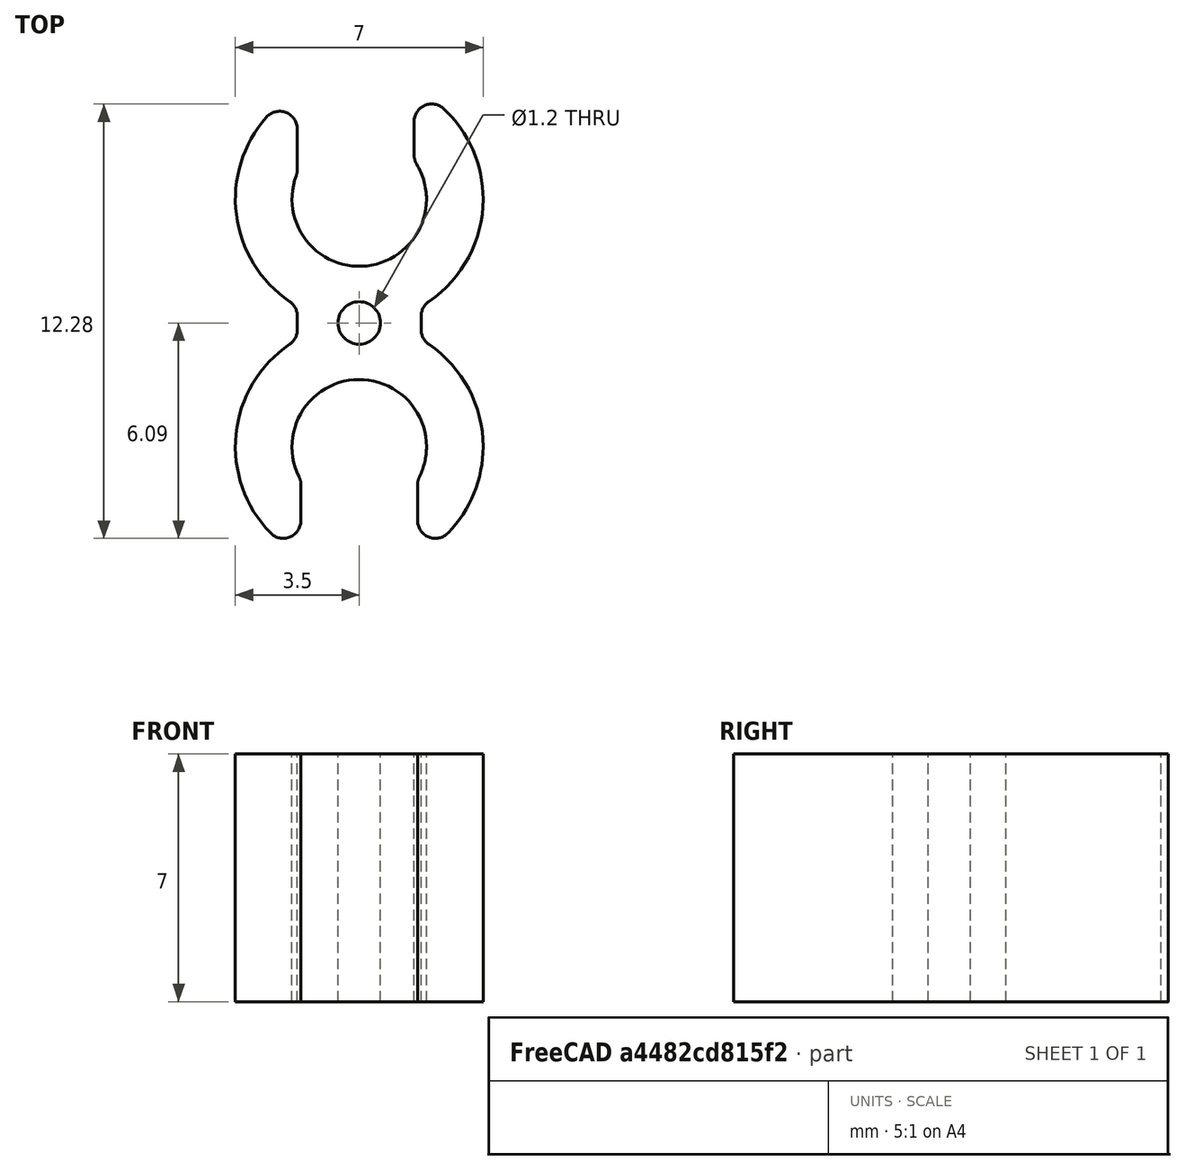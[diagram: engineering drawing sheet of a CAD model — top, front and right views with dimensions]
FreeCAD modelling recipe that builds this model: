
FCSTD DOCUMENT  (FreeCAD 0.15R4671 (Git))
Label: double_link
License: All rights reserved
LicenseURL: http://en.wikipedia.org/wiki/All_rights_reserved
objects: Part::Cut×4, Part::Cylinder×3, Part::Box×3, Part::MultiFuse×2, Part::FeaturePython×1, Part::Fillet×1
note: 14 computed .brp shape members not serialized (recipe doc carries the construction recipe); baked Part::Feature solids carry a one-line shape summary decoded from their .brp

FEATURE [Part::Cylinder] Cylinder  label="base_cylinder"
  Angle = 360
  Height = 7
  Radius = 3.5
FEATURE [Part::Cylinder] Cylinder001  label="base_cylinder_hole"
  Angle = 360
  Height = 10
  Placement = pos=(0,0,-1) rot=(0,0,1;0rad)
  Radius = 1.9
FEATURE [Part::Cut] Cut  label="cylinder_with_hole"
  Base = -> Cylinder
  Tool = -> Cylinder001
FEATURE [Part::FeaturePython] Clone  label="cylinder_with_hole2"  # Draft clone (typed FeaturePython)
  Objects = -> [Cut]
  Placement = pos=(0,7,0) rot=(0,0,1;0rad)
  Scale = (1,1,1)
FEATURE [Part::Box] Box  label="cylinder_open_section"
  Height = 10
  Length = 3.3
  Placement = pos=(-1.65,-10,-2) rot=(0,0,1;0rad)
  Width = 10
FEATURE [Part::Box] Box001  label="cylinder_open_section2"
  Height = 10
  Length = 3.3
  Placement = pos=(-1.65,7,-2) rot=(0,0,1;0rad)
  Width = 10
FEATURE [Part::Box] Box002  label="middle_union_piece"
  Height = 7
  Length = 3.5
  Placement = pos=(-1.75,2,0) rot=(0,0,1;0rad)
  Width = 3
FEATURE [Part::Cut] Cut001  label="open_cylinder_with_hole"
  Base = -> Cut
  Tool = -> Box
FEATURE [Part::Cut] Cut002  label="open_cylinder_with_hole2"
  Base = -> Clone
  Tool = -> Box001
FEATURE [Part::MultiFuse] Fusion  label="cylinder2_and_middle"
  Shapes = -> [Box002,Cut002]
FEATURE [Part::MultiFuse] Fusion001  label="cylinder1_cylinder2_and_middle"
  Shapes = -> [Fusion,Cut001]
FEATURE [Part::Fillet] Fillet  label="double_link"
  Base = -> Fusion001
  Edges = 12 edges r=0.5: [Edge2,Edge5,Edge9,Edge11,Edge15,Edge20,Edge23,Edge26,Edge28,Edge33,Edge36,Edge38]
FEATURE [Part::Cylinder] Cylinder002  label="double_link_hole"
  Angle = 360
  Height = 12
  Placement = pos=(0,3.5,-2) rot=(0,0,1;0rad)
  Radius = 0.6
FEATURE [Part::Cut] Cut003  label="double_link_with_hole"
  Base = -> Fillet
  Tool = -> Cylinder002
